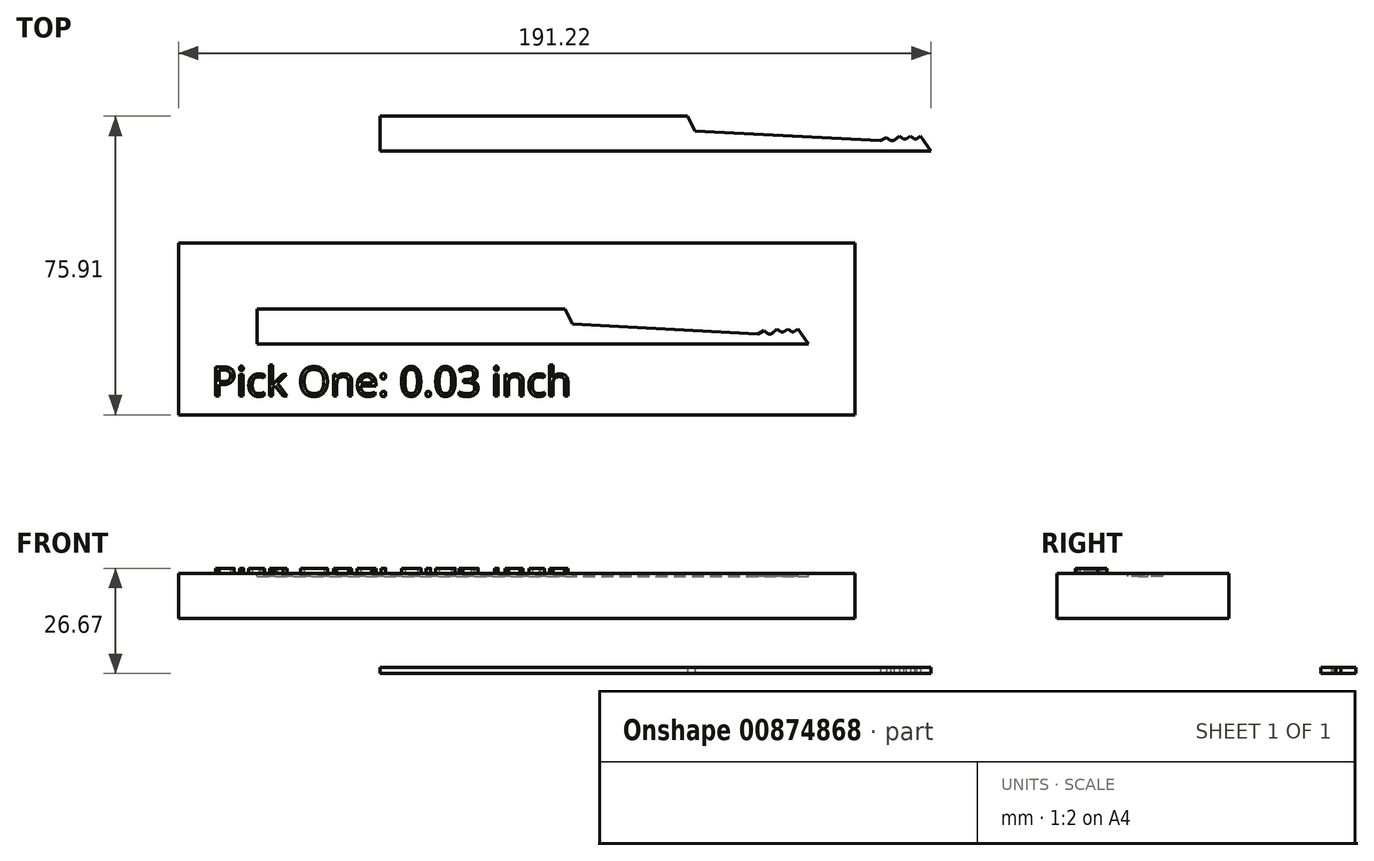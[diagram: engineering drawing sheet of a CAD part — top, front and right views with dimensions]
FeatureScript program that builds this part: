
annotation { "Feature Type Name" : "Feature", "Feature Type Description" : "" }
export const myFeature = defineFeature(function(context is Context, id is Id, definition is map)
    precondition{}
    {
        {
            var Q0;
            Q0=qCreatedBy(makeId("Top.planeOp"),FACE);
            var sketch = newSketch(context, id + "F0", { "sketchPlane" : qUnion([Q0])});
            skLineSegment(sketch, "E0", {"start": v(-80.01, 32.54) * mm, "end": v(0, 32.54) * mm});
            skLineSegment(sketch, "E1", {"start": v(0, 32.54) * mm, "end": v(60.03, 32.54) * mm});
            skLineSegment(sketch, "E2", {"start": v(57.33, 36.43) * mm, "end": v(60.03, 32.54) * mm});
            skLineSegment(sketch, "E3", {"start": v(57.33, 36.43) * mm, "end": v(56.26, 35.69) * mm});
            skLineSegment(sketch, "E4", {"start": v(56.26, 35.69) * mm, "end": v(55.77, 35.69) * mm});
            skLineSegment(sketch, "E5", {"start": v(55.77, 35.69) * mm, "end": v(54.8, 36.43) * mm});
            skLineSegment(sketch, "E6", {"start": v(54.8, 36.43) * mm, "end": v(53.6, 35.66) * mm});
            skLineSegment(sketch, "E7", {"start": v(53.6, 35.66) * mm, "end": v(53.03, 35.66) * mm});
            skLineSegment(sketch, "E8", {"start": v(53.03, 35.66) * mm, "end": v(52, 36.44) * mm});
            skLineSegment(sketch, "E9", {"start": v(52, 36.44) * mm, "end": v(50.63, 35.2) * mm});
            skLineSegment(sketch, "E10", {"start": v(50.63, 35.2) * mm, "end": v(49.76, 35.2) * mm});
            skLineSegment(sketch, "E11", {"start": v(49.76, 35.2) * mm, "end": v(48.7, 36) * mm});
            skLineSegment(sketch, "E12", {"start": v(48.7, 36) * mm, "end": v(47.22, 35.2) * mm});
            skLineSegment(sketch, "E13", {"start": v(47.22, 35.2) * mm, "end": v(0, 37.7) * mm});
            skLineSegment(sketch, "E14", {"start": v(-1.9, 41.47) * mm, "end": v(-0.76, 39.2) * mm});
            skLineSegment(sketch, "E15", {"start": v(-1.9, 41.47) * mm, "end": v(-80.01, 41.47) * mm});
            skLineSegment(sketch, "E16", {"start": v(-80.01, 41.47) * mm, "end": v(-80.01, 32.54) * mm});
            skLineSegment(sketch, "E17", {"start": v(-0.76, 39.2) * mm, "end": v(0, 37.7) * mm});
            skSolve(sketch);
        }
        {
            var Q0;
            Q0=makeQuery(id+"F0.imprint","IMPRINT",FACE,{"disambiguationData":[TD([[makeQuery(id+"F0.imprint","IMPRINT",EDGE,{"derivedFrom":sQuery(id+"F0.wireOp",EDGE,"E0")}),1.0]])]});
            extrude(context, id + "F1", {"entities" : qUnion([Q0]), "depth" : 1.52 * mm, "offsetDistance" : 25.4 * mm});
        }
        {
            var Q0;
            Q0=qCreatedBy(makeId("Top.planeOp"),FACE);
            var sketch = newSketch(context, id + "F2", { "sketchPlane" : qUnion([Q0])});
            skLineSegment(sketch, "E18.bottom", {"start": v(-97.4, 9.17) * mm, "end": v(85.17, 9.17) * mm});
            skLineSegment(sketch, "E18.top", {"start": v(-97.4, -34.44) * mm, "end": v(85.17, -34.44) * mm});
            skLineSegment(sketch, "E18.left", {"start": v(-97.4, 9.17) * mm, "end": v(-97.4, -34.44) * mm});
            skLineSegment(sketch, "E18.right", {"start": v(85.17, 9.17) * mm, "end": v(85.17, -34.44) * mm});
            skSolve(sketch);
        }
        {
            var Q0;
            Q0=makeQuery(id+"F2.imprint","IMPRINT",FACE,{"disambiguationData":[TD([[makeQuery(id+"F2.imprint","IMPRINT",EDGE,{"derivedFrom":sQuery(id+"F2.wireOp",EDGE,"E18.bottom")}),-1.0]])]});
            extrude(context, id + "F3", {"entities" : qUnion([Q0]), "depth" : 25.4 * mm, "offsetDistance" : 25.4 * mm});
        }
        {
            var Q0;
            Q0=makeQuery(id+"F3.opExtrude","CAP_FACE",FACE,{"disambiguationData":[OSD([sQuery(id+"F2.wireOp",EDGE,"E18.bottom"),sQuery(id+"F2.wireOp",EDGE,"E18.top"),sQuery(id+"F2.wireOp",EDGE,"E18.left"),sQuery(id+"F2.wireOp",EDGE,"E18.right")])],"isStart":false});
            var sketch = newSketch(context, id + "F4", { "sketchPlane" : qUnion([Q0])});
            skLineSegment(sketch, "E19", {"start": v(-111.13, -16.48) * mm, "end": v(-31.12, -16.48) * mm});
            skLineSegment(sketch, "E20", {"start": v(-31.12, -16.48) * mm, "end": v(28.9, -16.48) * mm});
            skLineSegment(sketch, "E21", {"start": v(26.2, -12.6) * mm, "end": v(28.9, -16.48) * mm});
            skLineSegment(sketch, "E22", {"start": v(26.2, -12.6) * mm, "end": v(25.14, -13.34) * mm});
            skLineSegment(sketch, "E23", {"start": v(25.14, -13.34) * mm, "end": v(24.65, -13.34) * mm});
            skLineSegment(sketch, "E24", {"start": v(24.65, -13.34) * mm, "end": v(23.67, -12.6) * mm});
            skLineSegment(sketch, "E25", {"start": v(23.67, -12.6) * mm, "end": v(22.48, -13.36) * mm});
            skLineSegment(sketch, "E26", {"start": v(22.48, -13.36) * mm, "end": v(21.9, -13.36) * mm});
            skLineSegment(sketch, "E27", {"start": v(21.9, -13.36) * mm, "end": v(20.87, -12.58) * mm});
            skLineSegment(sketch, "E28", {"start": v(20.87, -12.58) * mm, "end": v(19.5, -13.82) * mm});
            skLineSegment(sketch, "E29", {"start": v(19.5, -13.82) * mm, "end": v(18.64, -13.82) * mm});
            skLineSegment(sketch, "E30", {"start": v(18.64, -13.82) * mm, "end": v(17.57, -13.01) * mm});
            skLineSegment(sketch, "E31", {"start": v(17.57, -13.01) * mm, "end": v(16.1, -13.82) * mm});
            skLineSegment(sketch, "E32", {"start": v(16.1, -13.82) * mm, "end": v(-31.12, -11.33) * mm});
            skLineSegment(sketch, "E33", {"start": v(-33.03, -7.55) * mm, "end": v(-31.88, -9.83) * mm});
            skLineSegment(sketch, "E34", {"start": v(-33.03, -7.55) * mm, "end": v(-111.13, -7.55) * mm});
            skLineSegment(sketch, "E35", {"start": v(-111.13, -7.55) * mm, "end": v(-111.13, -16.48) * mm});
            skLineSegment(sketch, "E36", {"start": v(-31.88, -9.83) * mm, "end": v(-31.12, -11.33) * mm});
            skSolve(sketch);
        }
        {
            var Q0;
            Q0=makeQuery(id+"F3.opExtrude","SWEPT_FACE",FACE,{"disambiguationData":[OSD([sQuery(id+"F2.wireOp",EDGE,"E18.left")])]});
            extrude(context, id + "F5", {"entities" : qUnion([Q0]), "operationType" : NewBodyOperationType.ADD, "depth" : 33.78 * mm, "offsetDistance" : 25.4 * mm});
        }
        {
            var Q0;
            {var subQ0=sQuery(id+"F4.wireOp",EDGE,"E20");Q0=makeQuery(id+"F4.imprint","IMPRINT",FACE,{"disambiguationData":[TD([[makeQuery(id+"F4.imprint","IMPRINT",EDGE,{"derivedFrom":subQ0}),1.0]])]});}
            var Q1;
            {var subQ0=sQuery(id+"F4.wireOp",EDGE,"E35");Q1=makeQuery(id+"F4.imprint","IMPRINT",FACE,{"disambiguationData":[TD([[makeQuery(id+"F4.imprint","IMPRINT",EDGE,{"derivedFrom":subQ0}),1.0]])]});}
            extrude(context, id + "F6", {"entities" : qUnion([Q0, Q1]), "operationType" : NewBodyOperationType.REMOVE, "oppositeDirection" : true, "depth" : 0.76 * mm, "offsetDistance" : 25.4 * mm});
        }
        {
            var Q0;
            Q0=makeQuery(id+"F3.opExtrude","SWEPT_FACE",FACE,{"disambiguationData":[OSD([sQuery(id+"F2.wireOp",EDGE,"E18.right")])]});
            extrude(context, id + "F7", {"entities" : qUnion([Q0]), "operationType" : NewBodyOperationType.REMOVE, "oppositeDirection" : true, "depth" : 44.45 * mm, "offsetDistance" : 25.4 * mm});
        }
        {
            var Q0;
            {var subQ0=sQuery(id+"F2.wireOp",EDGE,"E18.left");Q0=makeQuery(id+"F5.boolean.opBoolean","MERGE",FACE,{"derivedFrom":[makeQuery(id+"F3.opExtrude","CAP_FACE",FACE,{"disambiguationData":[OSD([sQuery(id+"F2.wireOp",EDGE,"E18.bottom"),sQuery(id+"F2.wireOp",EDGE,"E18.top"),subQ0,sQuery(id+"F2.wireOp",EDGE,"E18.right")])],"isStart":true}),makeQuery(id+"F5.opExtrude","SWEPT_FACE",FACE,{"disambiguationData":[OSD([subQ0]),TDD([makeQuery(id+"F3.opExtrude","CAP_EDGE",EDGE,{"disambiguationData":[OSD([subQ0])],"isStart":true})])]})]});}
            extrude(context, id + "F8", {"entities" : qUnion([Q0]), "operationType" : NewBodyOperationType.REMOVE, "oppositeDirection" : true, "depth" : 13.97 * mm, "offsetDistance" : 25.4 * mm});
        }
        {
            var Q0;
            {var subQ0=sQuery(id+"F2.wireOp",EDGE,"E18.left");Q0=makeQuery(id+"F5.boolean.opBoolean","MERGE",FACE,{"derivedFrom":[makeQuery(id+"F3.opExtrude","CAP_FACE",FACE,{"disambiguationData":[OSD([sQuery(id+"F2.wireOp",EDGE,"E18.bottom"),sQuery(id+"F2.wireOp",EDGE,"E18.top"),subQ0,sQuery(id+"F2.wireOp",EDGE,"E18.right")])],"isStart":false}),makeQuery(id+"F5.opExtrude","SWEPT_FACE",FACE,{"disambiguationData":[OSD([subQ0]),TDD([makeQuery(id+"F3.opExtrude","CAP_EDGE",EDGE,{"disambiguationData":[OSD([subQ0])],"isStart":false})])]})]});}
            var sketch = newSketch(context, id + "F9", { "sketchPlane" : qUnion([Q0])});
            skText(sketch, "E37", { "text": "Pick One: 0.03 inch", "fontName": "OpenSans-Regular.ttf"});
            const initialGuessF9  = {"E37": [-0.12276, -0.02967, 1, 0, 0.00748]};
            skSetInitialGuess(sketch, initialGuessF9);
            skSolve(sketch);
        }
        {
            var Q0;
            Q0 = qSketchRegion(id + "F9", true);
            extrude(context, id + "F10", {"entities" : qUnion([Q0]), "operationType" : NewBodyOperationType.ADD, "depth" : 1.27 * mm, "offsetDistance" : 25.4 * mm});
        }
    });
